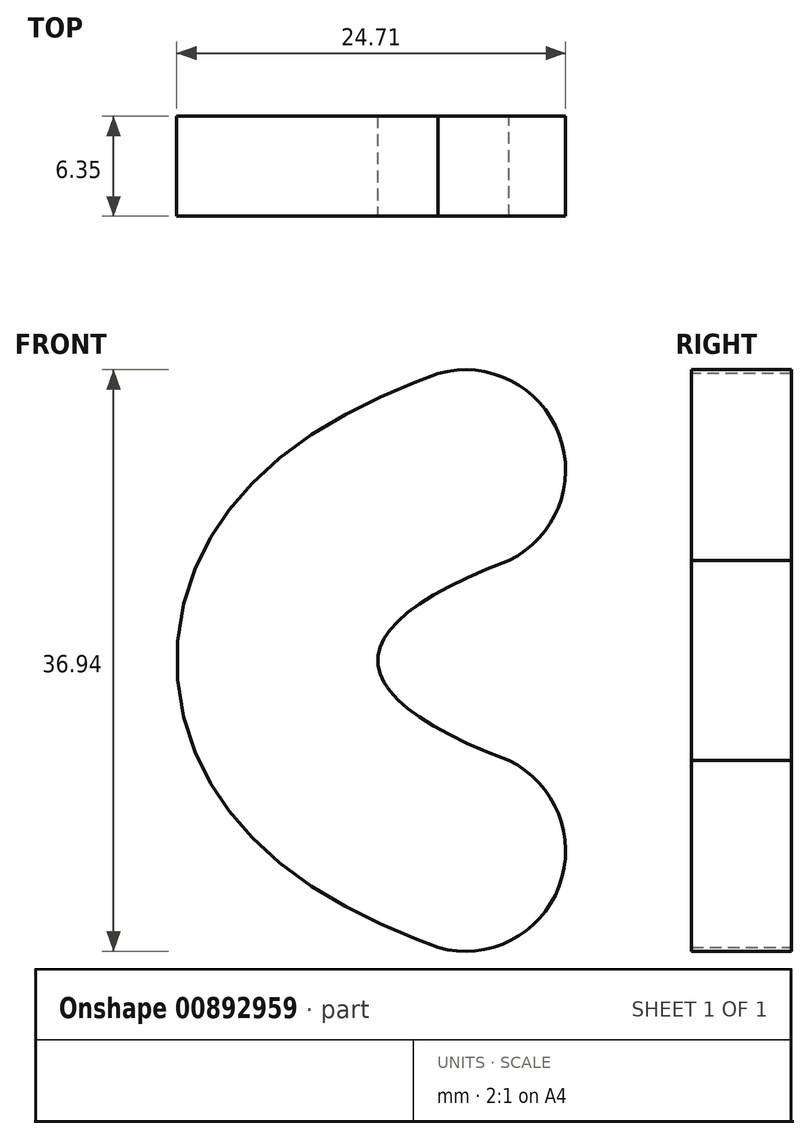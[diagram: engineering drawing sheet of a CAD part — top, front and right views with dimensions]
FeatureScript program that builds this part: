
annotation { "Feature Type Name" : "Feature", "Feature Type Description" : "" }
export const myFeature = defineFeature(function(context is Context, id is Id, definition is map)
    precondition{}
    {
        {
            var Q0;
            Q0=qCreatedBy(makeId("Front.planeOp"),FACE);
            var sketch = newSketch(context, id + "F0", { "sketchPlane" : qUnion([Q0])});
            skFitSpline(sketch, "E0", {"points": [v(0, 6.35) * mm, v(0, -6.35) * mm], "startDerivative": vector(-33.31, -12.58) * mm, "endDerivative": vector(33.31, -12.58) * mm});
            skFitSpline(sketch, "E1.0", {"points": [v(-4.49, 18.23) * mm, v(-5.35, 17.9) * mm, v(-7.02, 17.23) * mm, v(-9.4, 16.13) * mm, v(-11.7, 14.87) * mm, v(-13.95, 13.35) * mm, v(-15.85, 11.73) * mm, v(-17.36, 10.07) * mm, v(-18.45, 8.59) * mm, v(-19.47, 6.83) * mm, v(-20.32, 4.78) * mm, v(-20.9, 2.47) * mm, v(-21.1, 0) * mm, v(-20.9, -2.47) * mm, v(-20.32, -4.78) * mm, v(-19.47, -6.83) * mm, v(-18.45, -8.59) * mm, v(-17.36, -10.07) * mm, v(-15.85, -11.73) * mm, v(-13.95, -13.35) * mm, v(-11.7, -14.87) * mm, v(-9.4, -16.13) * mm, v(-7.02, -17.23) * mm, v(-5.35, -17.9) * mm, v(-4.49, -18.23) * mm]});
            skArc(sketch, "E2", {"start": v(0, 6.35) * mm, "mid": v(3.2, 14.34) * mm, "end": v(-4.49, 18.23) * mm});
            skArc(sketch, "E3", {"start": v(-4.49, -18.23) * mm, "mid": v(3.2, -14.34) * mm, "end": v(0, -6.35) * mm});
            skLineSegment(sketch, "E4", {"start": v(-8.33, 0) * mm, "end": v(-21.03, 0) * mm, "construction": true});
            skPoint(sketch, "E5", {"position": v(-20.96, 1.42) * mm});
            skArc(sketch, "E6.0", {"start": v(-0.81, 8.22) * mm, "mid": v(1.3, 13.63) * mm, "end": v(-3.86, 16.3) * mm});
            skFitSpline(sketch, "E6.1", {"points": [v(-0.72, 8.25) * mm, v(-2.16, 7.7) * mm, v(-4.08, 6.88) * mm, v(-6.17, 5.72) * mm, v(-7.52, 4.81) * mm, v(-8.64, 3.83) * mm, v(-9.55, 2.74) * mm, v(-10.2, 1.46) * mm, v(-10.44, 0) * mm, v(-10.2, -1.46) * mm, v(-9.55, -2.74) * mm, v(-8.64, -3.83) * mm, v(-7.52, -4.81) * mm, v(-6.17, -5.72) * mm, v(-4.08, -6.88) * mm, v(-2.16, -7.7) * mm, v(-0.72, -8.25) * mm]});
            skArc(sketch, "E6.2", {"start": v(-3.86, -16.3) * mm, "mid": v(1.3, -13.63) * mm, "end": v(-0.81, -8.22) * mm});
            skFitSpline(sketch, "E6.3", {"points": [v(-3.77, 16.33) * mm, v(-4.6, 16.01) * mm, v(-6.22, 15.37) * mm, v(-8.48, 14.31) * mm, v(-10.28, 13.32) * mm, v(-11.68, 12.43) * mm, v(-12.72, 11.68) * mm, v(-13.75, 10.85) * mm, v(-15.11, 9.57) * mm, v(-16.46, 7.98) * mm, v(-17.64, 5.93) * mm, v(-18.38, 4.14) * mm, v(-18.88, 2.14) * mm, v(-19.06, 0) * mm, v(-18.88, -2.14) * mm, v(-18.38, -4.14) * mm, v(-17.64, -5.93) * mm, v(-16.46, -7.98) * mm, v(-15.11, -9.57) * mm, v(-13.75, -10.85) * mm, v(-12.72, -11.68) * mm, v(-11.68, -12.43) * mm, v(-10.28, -13.32) * mm, v(-8.48, -14.31) * mm, v(-6.22, -15.37) * mm, v(-4.6, -16.01) * mm, v(-3.77, -16.33) * mm]});
            skSolve(sketch);
        }
        {
            var Q0;
            Q0=qSketchRegion(id+"F0",true);
            extrude(context, id + "F1", {"entities" : qUnion([Q0]), "depth" : 6.35 * mm, "offsetDistance" : 25.4 * mm});
        }
    });
